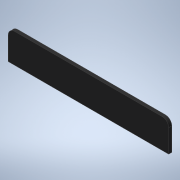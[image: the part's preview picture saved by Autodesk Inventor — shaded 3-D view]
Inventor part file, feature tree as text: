
AUTODESK INVENTOR PART (.ipt)
format: ipt  version: 2020 (Build 240168000, 168)  size: 102,400 bytes
history: native  units: mm
features: other x1, extrude x1, fillet x1
ambient origin geometry x8: Origin, YZ Plane, XZ Plane, XY Plane, X Axis, Y Axis, Z Axis, Center Point
bodies: Body1 (feature_tree)
feature tree (3):
  other  "實體1"
  extrude  "擠出1"  Depth=23.0mm
  fillet  "圓角1"  Radius=126.0mm
